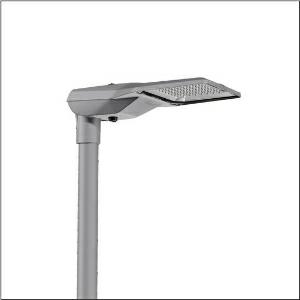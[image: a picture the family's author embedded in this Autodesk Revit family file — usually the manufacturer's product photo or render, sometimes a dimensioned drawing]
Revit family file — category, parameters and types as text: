
# Revit family: streetlight_sl_21_midi___stw1_0a_5xe3e23t08lb_dab2
name_source: partatom
category: Lighting Fixtures
units: mm (PartAtom-declared; Revit-internal decimal feet)

## family parameters
Cut with Voids When Loaded = No
Host = Face
Light Source = No
Part Type = Normal
Room Calculation Point = No
Round Connector Dimension = Use Diameter
Shared = No

## types (1)
- --- (1 x LED, 11880 lm, 99.6 W, 2200K)
    Apparent Load = 100 VA
    CIE Flux Codes = 38 75 98 100 100
    Color Rendering = 70
    Color Temperature = 2200K
    Default Elevation = 1800 mm
    Description = Streetlight SL 21 midi, mast luminaire, primary light control with lens, of PMMA, primary optical cover: cover, of toughened safety glass, transparent, light distribution: STW1.0a, light emission: direct distribution, primary light characteristic: asymmetric, installation type: side-entry, post-top, LED, High Power LED, rated luminous flux: 11.880lm, luminous efficacy: 119lm/W, light colour: 722, colour temperature: 2200K, control gear: D4i, control: overheat protection, constant luminous flux control, time-dependent luminous flux control, flexible luminous flux parameterisation, pre-setting: logarithmic dimming characteristic, mains connection: 230..240V, AC, 50/60Hz, start of lifetime: 100W, end of service life: 102W, reduction: 45W, luminaire housing, of diecast aluminium, powder-coated, Siteco® metallic grey (DB 702S), corrosivity category C5 mid according to DIN EN ISO 12944, please order mast flange separately, inclination adjustable: 0°, 5°, 10°, 15°, sealing non-destructively replaceable, multi-level sealing system, length: 644mm, width: 335mm, height: 110mm, mast flange for spigot size: 42mm (side-entry): 5XC10008XM4, 60/48mm (side-entry/post-top): 5XC10108XM2, 76/60mm (side-entry/post-top): 5XC10108XM1, mounting height: 4..8m, Smart Interface below and above, protection rating (complete): IP66, insulation class (complete): insulation class II (safety insulation), certification: CE, ENEC, ENEC+, VDE, impact resistance: IK10, permissible operating ambient temperature for outdoor applications: -40..+50°C, standard-compliant lighting for roads and squares, packaging unit: 1 piece

Light Distribution: STW1.0a
    Height = 111 mm
    Lamp = 1 x LED
    Lamp Light Flux = 11880 lm
    Lamp Power = 99.6 W
    Lamp count = 1
    Length = 644 mm
    Luminous efficacy = 119 lm/W
    Manufacturer = Siteco
    ModVariant = No
    Model = 5XE3E23T08LB
    Number of Poles = 1
    OnlyDefault = Yes
    Power Factor = 1
    Product Name = Streetlight SL 21 midi | STW1.0a
    Product group = mast luminaire | pylon top
    ProductGroupID = 6100
    Protection Class = Protection class II
    Protection Degree = IP 66
    RLX_Detail_Level = 1
    RLX_Emergency_Light_Flux = 0 lm
    RLX_Emergency_Type = 0
    RLX_Emergency_Type_DB = No
    RlxData = <blob elided: 26953 chars, md5=2618d714>
    Socket = socket
    Standby Power = 0 W
    System Light Flux = 11880 lm
    System Power = 100 W
    Type Comments = factory setting: luminous flux: 100 % | dim-lin: 254 | 1020 mA
    Type Image = l_1004304.jpg
    URL = http://relux.com
    VarID = @adj_011985
    Voltage = 0 V
    Weight = 0.00 kg
    Width = 336 mm

## geometry (parser evidence)
native form markers: Blend x4, Sweep x10
no freeform markers — native parametric forms only
